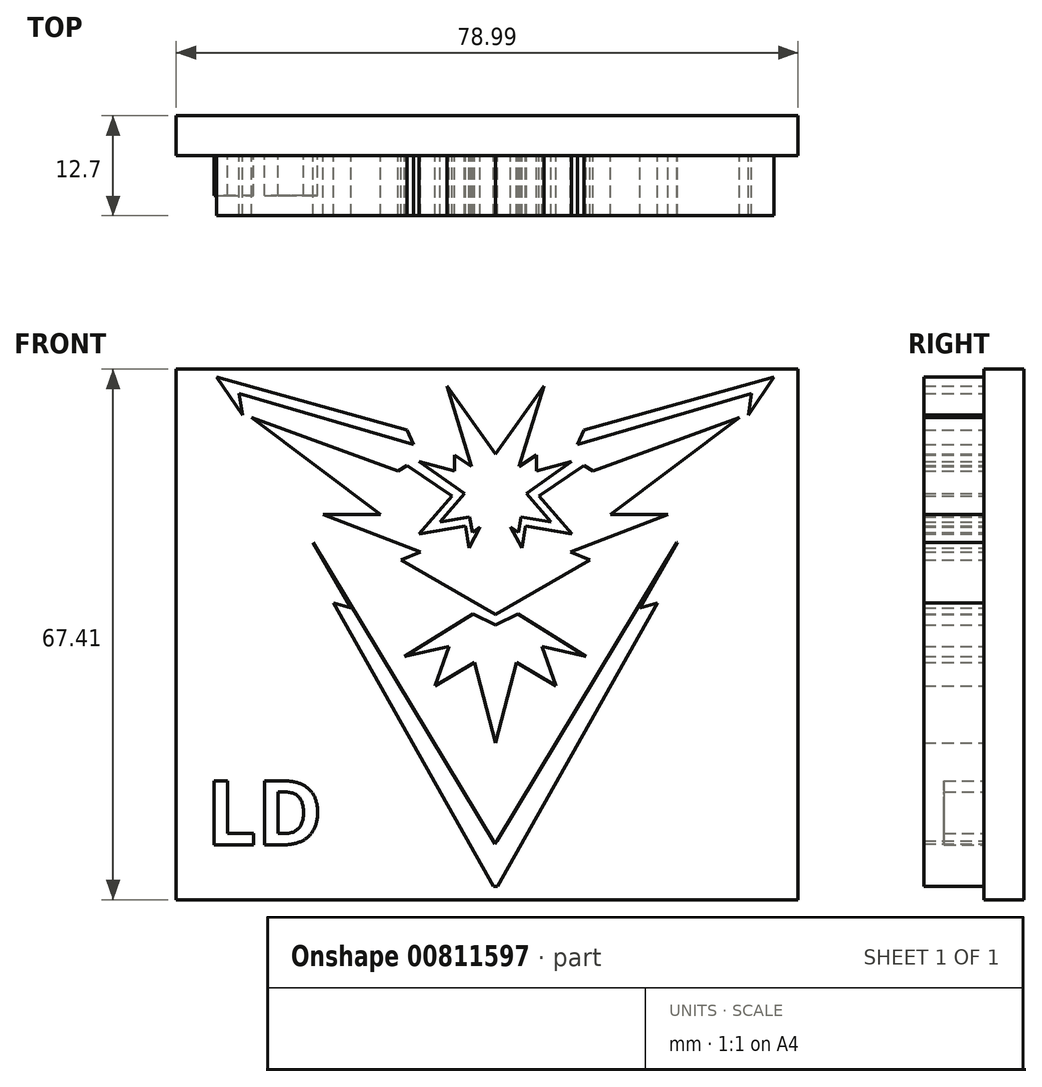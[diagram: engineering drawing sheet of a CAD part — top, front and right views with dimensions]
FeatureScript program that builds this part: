
annotation { "Feature Type Name" : "Feature", "Feature Type Description" : "" }
export const myFeature = defineFeature(function(context is Context, id is Id, definition is map)
    precondition{}
    {
        {
            var Q0;
            Q0=qCreatedBy(makeId("Front.planeOp"),FACE);
            var sketch = newSketch(context, id + "F0", { "sketchPlane" : qUnion([Q0])});
            skLineSegment(sketch, "E0", {"start": v(1.5, 35.4) * mm, "end": v(-4.67, 44.05) * mm});
            skLineSegment(sketch, "E1", {"start": v(-4.67, 44.05) * mm, "end": v(-1.5, 33.83) * mm});
            skLineSegment(sketch, "E2", {"start": v(-1.5, 33.83) * mm, "end": v(-3.69, 35.28) * mm});
            skLineSegment(sketch, "E3", {"start": v(-3.69, 35.28) * mm, "end": v(-3.69, 33.23) * mm});
            skLineSegment(sketch, "E4", {"start": v(-3.69, 33.23) * mm, "end": v(-8.18, 34.47) * mm});
            skLineSegment(sketch, "E5", {"start": v(-8.18, 34.47) * mm, "end": v(-2.45, 30.4) * mm});
            skLineSegment(sketch, "E6", {"start": v(-2.45, 30.4) * mm, "end": v(-5.53, 26.76) * mm});
            skLineSegment(sketch, "E7", {"start": v(-5.53, 26.76) * mm, "end": v(-1.76, 27.4) * mm});
            skLineSegment(sketch, "E8", {"start": v(-1.76, 27.4) * mm, "end": v(-1.42, 25.4) * mm});
            skLineSegment(sketch, "E9", {"start": v(-1.42, 25.4) * mm, "end": v(-0.44, 26.12) * mm});
            skLineSegment(sketch, "E10", {"start": v(-0.44, 26.12) * mm, "end": v(-1.85, 23.47) * mm});
            skLineSegment(sketch, "E11", {"start": v(-1.85, 23.47) * mm, "end": v(-2.32, 26.25) * mm});
            skLineSegment(sketch, "E12", {"start": v(-2.32, 26.25) * mm, "end": v(-8.22, 25.25) * mm});
            skLineSegment(sketch, "E13", {"start": v(-8.22, 25.25) * mm, "end": v(-4.03, 30.06) * mm});
            skLineSegment(sketch, "E14", {"start": v(-4.03, 30.06) * mm, "end": v(-9.72, 33.91) * mm});
            skLineSegment(sketch, "E15", {"start": v(-9.72, 33.91) * mm, "end": v(-10.88, 33.23) * mm});
            skLineSegment(sketch, "E16", {"start": v(-10.88, 33.23) * mm, "end": v(-29.5, 40.03) * mm});
            skLineSegment(sketch, "E17", {"start": v(-29.5, 40.03) * mm, "end": v(-13.1, 27.7) * mm});
            skLineSegment(sketch, "E18", {"start": v(-13.1, 27.7) * mm, "end": v(-20.38, 27.7) * mm});
            skLineSegment(sketch, "E19", {"start": v(-20.38, 27.7) * mm, "end": v(-8.01, 22.95) * mm});
            skLineSegment(sketch, "E20", {"start": v(-8.01, 22.95) * mm, "end": v(-10.5, 21.93) * mm});
            skLineSegment(sketch, "E21", {"start": v(-10.5, 21.93) * mm, "end": v(1.5, 15.01) * mm});
            skLineSegment(sketch, "E22", {"start": v(-1.35, 15.06) * mm, "end": v(-10.01, 9.67) * mm});
            skLineSegment(sketch, "E23", {"start": v(-10.01, 9.67) * mm, "end": v(-4.38, 10.97) * mm});
            skLineSegment(sketch, "E24", {"start": v(-4.38, 10.97) * mm, "end": v(-6.2, 5.95) * mm});
            skLineSegment(sketch, "E25", {"start": v(-6.2, 5.95) * mm, "end": v(-1.17, 8.91) * mm});
            skLineSegment(sketch, "E26", {"start": v(-1.17, 8.91) * mm, "end": v(1.5, -1.33) * mm});
            skLineSegment(sketch, "E27", {"start": v(-1.35, 15.06) * mm, "end": v(1.5, 13.7) * mm});
            skLineSegment(sketch, "E28", {"start": v(-33.9, 45.2) * mm, "end": v(-30.64, 40.35) * mm});
            skLineSegment(sketch, "E29", {"start": v(-30.64, 40.35) * mm, "end": v(-31.05, 43.05) * mm});
            skLineSegment(sketch, "E30", {"start": v(-31.05, 43.05) * mm, "end": v(-8.9, 36.6) * mm});
            skLineSegment(sketch, "E31", {"start": v(-8.9, 36.6) * mm, "end": v(-9.75, 38.47) * mm});
            skLineSegment(sketch, "E32", {"start": v(-9.75, 38.47) * mm, "end": v(-33.9, 45.2) * mm});
            skLineSegment(sketch, "E33", {"start": v(-21.64, 24.13) * mm, "end": v(-16.86, 15.86) * mm});
            skLineSegment(sketch, "E34", {"start": v(-16.86, 15.86) * mm, "end": v(-19.05, 16.5) * mm});
            skLineSegment(sketch, "E35", {"start": v(-19.05, 16.5) * mm, "end": v(1.24, -19.55) * mm});
            skLineSegment(sketch, "E36", {"start": v(-21.64, 24.13) * mm, "end": v(1.24, -13.77) * mm});
            skLineSegment(sketch, "E37.MirrorCS", {"start": v(22.07, 16.5) * mm, "end": v(1.78, -19.55) * mm});
            skLineSegment(sketch, "E38.MirrorCS", {"start": v(24.59, 24.18) * mm, "end": v(1.7, -13.72) * mm});
            skLineSegment(sketch, "E39.MirrorCS", {"start": v(19.88, 15.86) * mm, "end": v(22.07, 16.5) * mm});
            skLineSegment(sketch, "E40.MirrorCS", {"start": v(24.66, 24.13) * mm, "end": v(19.88, 15.86) * mm});
            skLineSegment(sketch, "E41.MirrorCS", {"start": v(4.37, 15.06) * mm, "end": v(13.02, 9.67) * mm});
            skLineSegment(sketch, "E42.MirrorCS", {"start": v(13.02, 9.67) * mm, "end": v(7.4, 10.97) * mm});
            skLineSegment(sketch, "E43.MirrorCS", {"start": v(9.21, 5.95) * mm, "end": v(4.19, 8.91) * mm});
            skLineSegment(sketch, "E44.MirrorCS", {"start": v(7.4, 10.97) * mm, "end": v(9.21, 5.95) * mm});
            skLineSegment(sketch, "E45.MirrorCS", {"start": v(4.19, 8.91) * mm, "end": v(1.5, -1.33) * mm});
            skLineSegment(sketch, "E46.MirrorCS", {"start": v(4.37, 15.06) * mm, "end": v(1.5, 13.7) * mm});
            skLineSegment(sketch, "E47.MirrorCS", {"start": v(13.5, 21.93) * mm, "end": v(1.5, 15.01) * mm});
            skLineSegment(sketch, "E48.MirrorCS", {"start": v(11.03, 22.95) * mm, "end": v(13.5, 21.93) * mm});
            skLineSegment(sketch, "E49.MirrorCS", {"start": v(23.4, 27.7) * mm, "end": v(11.03, 22.95) * mm});
            skLineSegment(sketch, "E50.MirrorCS", {"start": v(16.12, 27.7) * mm, "end": v(23.4, 27.7) * mm});
            skLineSegment(sketch, "E51.MirrorCS", {"start": v(32.51, 40.03) * mm, "end": v(16.12, 27.7) * mm});
            skLineSegment(sketch, "E52.MirrorCS", {"start": v(13.9, 33.23) * mm, "end": v(32.51, 40.03) * mm});
            skLineSegment(sketch, "E53.MirrorCS", {"start": v(12.74, 33.91) * mm, "end": v(13.9, 33.23) * mm});
            skLineSegment(sketch, "E54.MirrorCS", {"start": v(7.05, 30.06) * mm, "end": v(12.74, 33.91) * mm});
            skLineSegment(sketch, "E55.MirrorCS", {"start": v(11.24, 25.25) * mm, "end": v(7.05, 30.06) * mm});
            skLineSegment(sketch, "E56.MirrorCS", {"start": v(5.33, 26.25) * mm, "end": v(11.24, 25.25) * mm});
            skLineSegment(sketch, "E57.MirrorCS", {"start": v(4.86, 23.47) * mm, "end": v(5.33, 26.25) * mm});
            skLineSegment(sketch, "E58.MirrorCS", {"start": v(3.45, 26.12) * mm, "end": v(4.86, 23.47) * mm});
            skLineSegment(sketch, "E59.MirrorCS", {"start": v(4.44, 25.4) * mm, "end": v(3.45, 26.12) * mm});
            skLineSegment(sketch, "E60.MirrorCS", {"start": v(4.78, 27.4) * mm, "end": v(4.44, 25.4) * mm});
            skLineSegment(sketch, "E61.MirrorCS", {"start": v(8.54, 26.76) * mm, "end": v(4.78, 27.4) * mm});
            skLineSegment(sketch, "E62.MirrorCS", {"start": v(5.46, 30.4) * mm, "end": v(8.54, 26.76) * mm});
            skLineSegment(sketch, "E63.MirrorCS", {"start": v(11.2, 34.47) * mm, "end": v(5.46, 30.4) * mm});
            skLineSegment(sketch, "E64.MirrorCS", {"start": v(6.7, 33.23) * mm, "end": v(11.2, 34.47) * mm});
            skLineSegment(sketch, "E65.MirrorCS", {"start": v(6.7, 35.28) * mm, "end": v(6.7, 33.23) * mm});
            skLineSegment(sketch, "E66.MirrorCS", {"start": v(4.52, 33.83) * mm, "end": v(6.7, 35.28) * mm});
            skLineSegment(sketch, "E67.MirrorCS", {"start": v(7.69, 44.05) * mm, "end": v(4.52, 33.83) * mm});
            skLineSegment(sketch, "E68.MirrorCS", {"start": v(1.5, 35.4) * mm, "end": v(7.69, 44.05) * mm});
            skLineSegment(sketch, "E69.MirrorCS", {"start": v(34.06, 43.05) * mm, "end": v(11.91, 36.6) * mm});
            skLineSegment(sketch, "E70.MirrorCS", {"start": v(12.76, 38.47) * mm, "end": v(36.91, 45.2) * mm});
            skLineSegment(sketch, "E71.MirrorCS", {"start": v(11.91, 36.6) * mm, "end": v(12.76, 38.47) * mm});
            skLineSegment(sketch, "E72.MirrorCS", {"start": v(33.65, 40.35) * mm, "end": v(34.06, 43.05) * mm});
            skLineSegment(sketch, "E73.MirrorCS", {"start": v(36.91, 45.2) * mm, "end": v(33.65, 40.35) * mm});
            skLineSegment(sketch, "E74", {"start": v(1.24, -13.77) * mm, "end": v(1.47, -14.16) * mm});
            skLineSegment(sketch, "E75", {"start": v(1.47, -14.16) * mm, "end": v(1.7, -13.72) * mm});
            skLineSegment(sketch, "E76", {"start": v(1.24, -19.55) * mm, "end": v(1.78, -19.55) * mm});
            skLineSegment(sketch, "E77", {"start": v(24.59, 24.18) * mm, "end": v(24.66, 24.13) * mm});
            skSolve(sketch);
        }
        {
            var Q0;
            Q0=makeQuery(id+"F0.imprint","IMPRINT",FACE,{"disambiguationData":[TD([[makeQuery(id+"F0.imprint","IMPRINT",EDGE,{"derivedFrom":sQuery(id+"F0.wireOp",EDGE,"E69.MirrorCS")}),-1.0]])]});
            var Q1;
            Q1=makeQuery(id+"F0.imprint","IMPRINT",FACE,{"disambiguationData":[TD([[makeQuery(id+"F0.imprint","IMPRINT",EDGE,{"derivedFrom":sQuery(id+"F0.wireOp",EDGE,"E33")}),1.0]])]});
            var Q2;
            Q2=makeQuery(id+"F0.imprint","IMPRINT",FACE,{"disambiguationData":[TD([[makeQuery(id+"F0.imprint","IMPRINT",EDGE,{"derivedFrom":sQuery(id+"F0.wireOp",EDGE,"E22")}),1.0]])]});
            var Q3;
            Q3=makeQuery(id+"F0.imprint","IMPRINT",FACE,{"disambiguationData":[TD([[makeQuery(id+"F0.imprint","IMPRINT",EDGE,{"derivedFrom":sQuery(id+"F0.wireOp",EDGE,"E28")}),1.0]])]});
            var Q4;
            Q4=makeQuery(id+"F0.imprint","IMPRINT",FACE,{"disambiguationData":[TD([[makeQuery(id+"F0.imprint","IMPRINT",EDGE,{"derivedFrom":sQuery(id+"F0.wireOp",EDGE,"E0")}),1.0]])]});
            extrude(context, id + "F1", {"entities" : qUnion([Q0, Q1, Q2, Q3, Q4]), "depth" : 7.62 * mm});
        }
        {
            var Q0;
            Q0=makeQuery(id+"F1.opExtrude","CAP_FACE",FACE,{"disambiguationData":[OSD([sQuery(id+"F0.wireOp",EDGE,"E0"),sQuery(id+"F0.wireOp",EDGE,"E1"),sQuery(id+"F0.wireOp",EDGE,"E2"),sQuery(id+"F0.wireOp",EDGE,"E3"),sQuery(id+"F0.wireOp",EDGE,"E4"),sQuery(id+"F0.wireOp",EDGE,"E5"),sQuery(id+"F0.wireOp",EDGE,"E6"),sQuery(id+"F0.wireOp",EDGE,"E7"),sQuery(id+"F0.wireOp",EDGE,"E8"),sQuery(id+"F0.wireOp",EDGE,"E9"),sQuery(id+"F0.wireOp",EDGE,"E10"),sQuery(id+"F0.wireOp",EDGE,"E11"),sQuery(id+"F0.wireOp",EDGE,"E12"),sQuery(id+"F0.wireOp",EDGE,"E13"),sQuery(id+"F0.wireOp",EDGE,"E14"),sQuery(id+"F0.wireOp",EDGE,"E15"),sQuery(id+"F0.wireOp",EDGE,"E16"),sQuery(id+"F0.wireOp",EDGE,"E17"),sQuery(id+"F0.wireOp",EDGE,"E18"),sQuery(id+"F0.wireOp",EDGE,"E19"),sQuery(id+"F0.wireOp",EDGE,"E20"),sQuery(id+"F0.wireOp",EDGE,"E21"),sQuery(id+"F0.wireOp",EDGE,"E47.MirrorCS"),sQuery(id+"F0.wireOp",EDGE,"E48.MirrorCS"),sQuery(id+"F0.wireOp",EDGE,"E49.MirrorCS"),sQuery(id+"F0.wireOp",EDGE,"E50.MirrorCS"),sQuery(id+"F0.wireOp",EDGE,"E51.MirrorCS"),sQuery(id+"F0.wireOp",EDGE,"E52.MirrorCS"),sQuery(id+"F0.wireOp",EDGE,"E53.MirrorCS"),sQuery(id+"F0.wireOp",EDGE,"E54.MirrorCS"),sQuery(id+"F0.wireOp",EDGE,"E55.MirrorCS"),sQuery(id+"F0.wireOp",EDGE,"E56.MirrorCS"),sQuery(id+"F0.wireOp",EDGE,"E57.MirrorCS"),sQuery(id+"F0.wireOp",EDGE,"E58.MirrorCS"),sQuery(id+"F0.wireOp",EDGE,"E59.MirrorCS"),sQuery(id+"F0.wireOp",EDGE,"E60.MirrorCS"),sQuery(id+"F0.wireOp",EDGE,"E61.MirrorCS"),sQuery(id+"F0.wireOp",EDGE,"E62.MirrorCS"),sQuery(id+"F0.wireOp",EDGE,"E63.MirrorCS"),sQuery(id+"F0.wireOp",EDGE,"E64.MirrorCS"),sQuery(id+"F0.wireOp",EDGE,"E65.MirrorCS"),sQuery(id+"F0.wireOp",EDGE,"E66.MirrorCS"),sQuery(id+"F0.wireOp",EDGE,"E67.MirrorCS"),sQuery(id+"F0.wireOp",EDGE,"E68.MirrorCS")])],"isStart":true});
            var sketch = newSketch(context, id + "F2", { "sketchPlane" : qUnion([Q0])});
            skLineSegment(sketch, "E78.bottom", {"start": v(-39.95, 46.17) * mm, "end": v(39.04, 46.17) * mm});
            skLineSegment(sketch, "E78.top", {"start": v(-39.95, -21.24) * mm, "end": v(39.04, -21.24) * mm});
            skLineSegment(sketch, "E78.left", {"start": v(-39.95, 46.17) * mm, "end": v(-39.95, -21.24) * mm});
            skLineSegment(sketch, "E78.right", {"start": v(39.04, 46.17) * mm, "end": v(39.04, -21.24) * mm});
            skSolve(sketch);
        }
        {
            var Q0;
            Q0 = qSketchRegion(id + "F2", true);
            extrude(context, id + "F3", {"entities" : qUnion([Q0]), "depth" : 5.08 * mm, "offsetDistance" : 25.4 * mm});
        }
        {
            var Q0;
            Q0=makeQuery(id+"F3.opExtrude","CAP_FACE",FACE,{"disambiguationData":[OSD([sQuery(id+"F2.wireOp",EDGE,"E78.bottom"),sQuery(id+"F2.wireOp",EDGE,"E78.top"),sQuery(id+"F2.wireOp",EDGE,"E78.left"),sQuery(id+"F2.wireOp",EDGE,"E78.right")])],"isStart":true});
            var sketch = newSketch(context, id + "F4", { "sketchPlane" : qUnion([Q0])});
            skText(sketch, "E79", { "text": "LD", "fontName": "OpenSans-Bold.ttf"});
            const initialGuessF4  = {"E79": [-0.03525, -0.01425, 1, 0, 0.00818]};
            skSetInitialGuess(sketch, initialGuessF4);
            skSolve(sketch);
        }
        {
            var Q0;
            Q0 = qSketchRegion(id + "F4", true);
            extrude(context, id + "F5", {"entities" : qUnion([Q0]), "operationType" : NewBodyOperationType.ADD, "depth" : 5.08 * mm, "offsetDistance" : 25.4 * mm});
        }
        {
            var Q0;
            Q0 = qSketchRegion(id + "F4", true);
            extrude(context, id + "F6", {"entities" : qUnion([Q0]), "operationType" : NewBodyOperationType.ADD, "depth" : 2.54 * mm, "offsetDistance" : 25.4 * mm});
        }
    });
